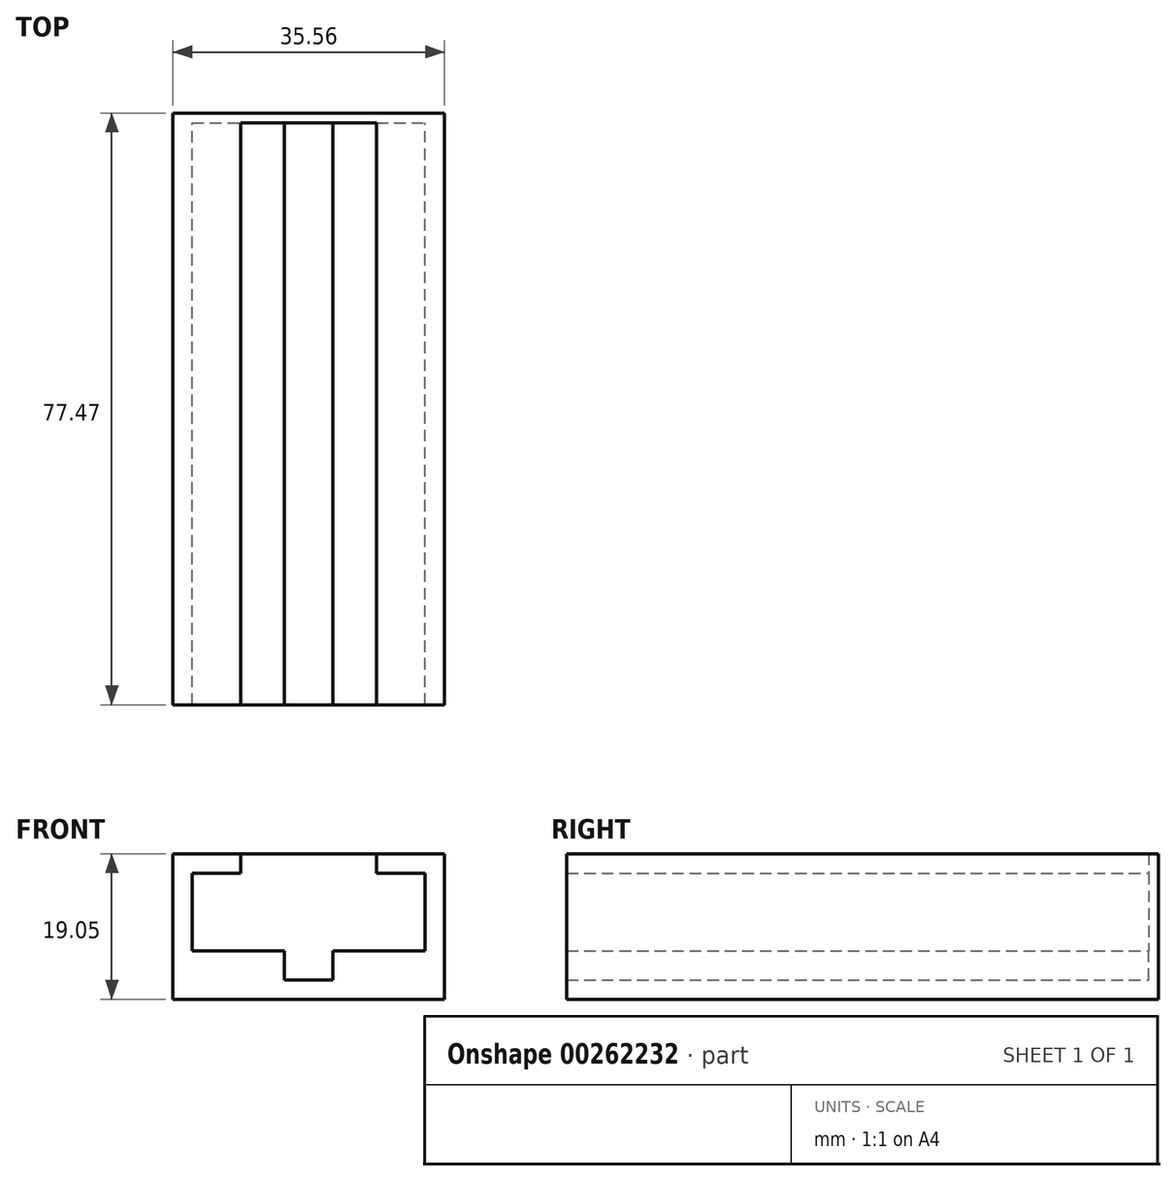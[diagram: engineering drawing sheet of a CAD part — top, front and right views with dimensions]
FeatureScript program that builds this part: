
annotation { "Feature Type Name" : "Feature", "Feature Type Description" : "" }
export const myFeature = defineFeature(function(context is Context, id is Id, definition is map)
    precondition{}
    {
        {
            var Q0;
            Q0=qCreatedBy(makeId("Front.planeOp"),FACE);
            var sketch = newSketch(context, id + "F0", { "sketchPlane" : qUnion([Q0])});
            skLineSegment(sketch, "E0.top", {"start": v(-70.8, -28.89) * mm, "end": v(-35.24, -28.89) * mm});
            skLineSegment(sketch, "E0.left", {"start": v(-70.8, -22.54) * mm, "end": v(-70.8, -28.89) * mm});
            skLineSegment(sketch, "E0.right", {"start": v(-35.24, -22.54) * mm, "end": v(-35.24, -28.89) * mm});
            skLineSegment(sketch, "E1", {"start": v(-70.8, -22.54) * mm, "end": v(-70.8, -9.84) * mm});
            skLineSegment(sketch, "E2", {"start": v(-70.8, -9.84) * mm, "end": v(-61.91, -9.84) * mm});
            skLineSegment(sketch, "E3", {"start": v(-61.91, -9.84) * mm, "end": v(-61.91, -12.38) * mm});
            skLineSegment(sketch, "E4", {"start": v(-61.91, -12.38) * mm, "end": v(-68.26, -12.38) * mm});
            skLineSegment(sketch, "E5", {"start": v(-35.24, -22.54) * mm, "end": v(-35.24, -9.84) * mm});
            skLineSegment(sketch, "E6", {"start": v(-35.24, -9.84) * mm, "end": v(-44.13, -9.84) * mm});
            skLineSegment(sketch, "E7", {"start": v(-44.13, -9.84) * mm, "end": v(-44.13, -12.38) * mm});
            skLineSegment(sketch, "E8", {"start": v(-44.13, -12.38) * mm, "end": v(-37.78, -12.38) * mm});
            skLineSegment(sketch, "E9", {"start": v(-61.91, -9.84) * mm, "end": v(-44.13, -9.84) * mm});
            skLineSegment(sketch, "E10", {"start": v(-68.26, -12.38) * mm, "end": v(-68.26, -22.54) * mm});
            skLineSegment(sketch, "E11", {"start": v(-68.26, -22.54) * mm, "end": v(-56.2, -22.54) * mm});
            skLineSegment(sketch, "E12.trimOffspring", {"start": v(-49.85, -22.54) * mm, "end": v(-37.78, -22.54) * mm});
            skLineSegment(sketch, "E13", {"start": v(-37.78, -12.38) * mm, "end": v(-37.78, -22.54) * mm});
            skLineSegment(sketch, "E14", {"start": v(-56.2, -26.35) * mm, "end": v(-49.85, -26.35) * mm});
            skLineSegment(sketch, "E15", {"start": v(-56.2, -26.35) * mm, "end": v(-56.2, -22.54) * mm});
            skLineSegment(sketch, "E16", {"start": v(-49.85, -26.35) * mm, "end": v(-49.85, -22.54) * mm});
            skSolve(sketch);
        }
        {
            var Q0;
            Q0=makeQuery(id+"F0.imprint","IMPRINT",FACE,{"disambiguationData":[TD([[makeQuery(id+"F0.imprint","IMPRINT",EDGE,{"derivedFrom":sQuery(id+"F0.wireOp",EDGE,"E0.top")}),1.0]])]});
            extrude(context, id + "F1", {"entities" : qUnion([Q0]), "depth" : 77.47 * mm});
        }
        {
            var Q0;
            Q0 = qSketchRegion(id + "F0", true);
            extrude(context, id + "F2", {"entities" : qUnion([Q0]), "operationType" : NewBodyOperationType.ADD, "depth" : 1.27 * mm});
        }
    });
